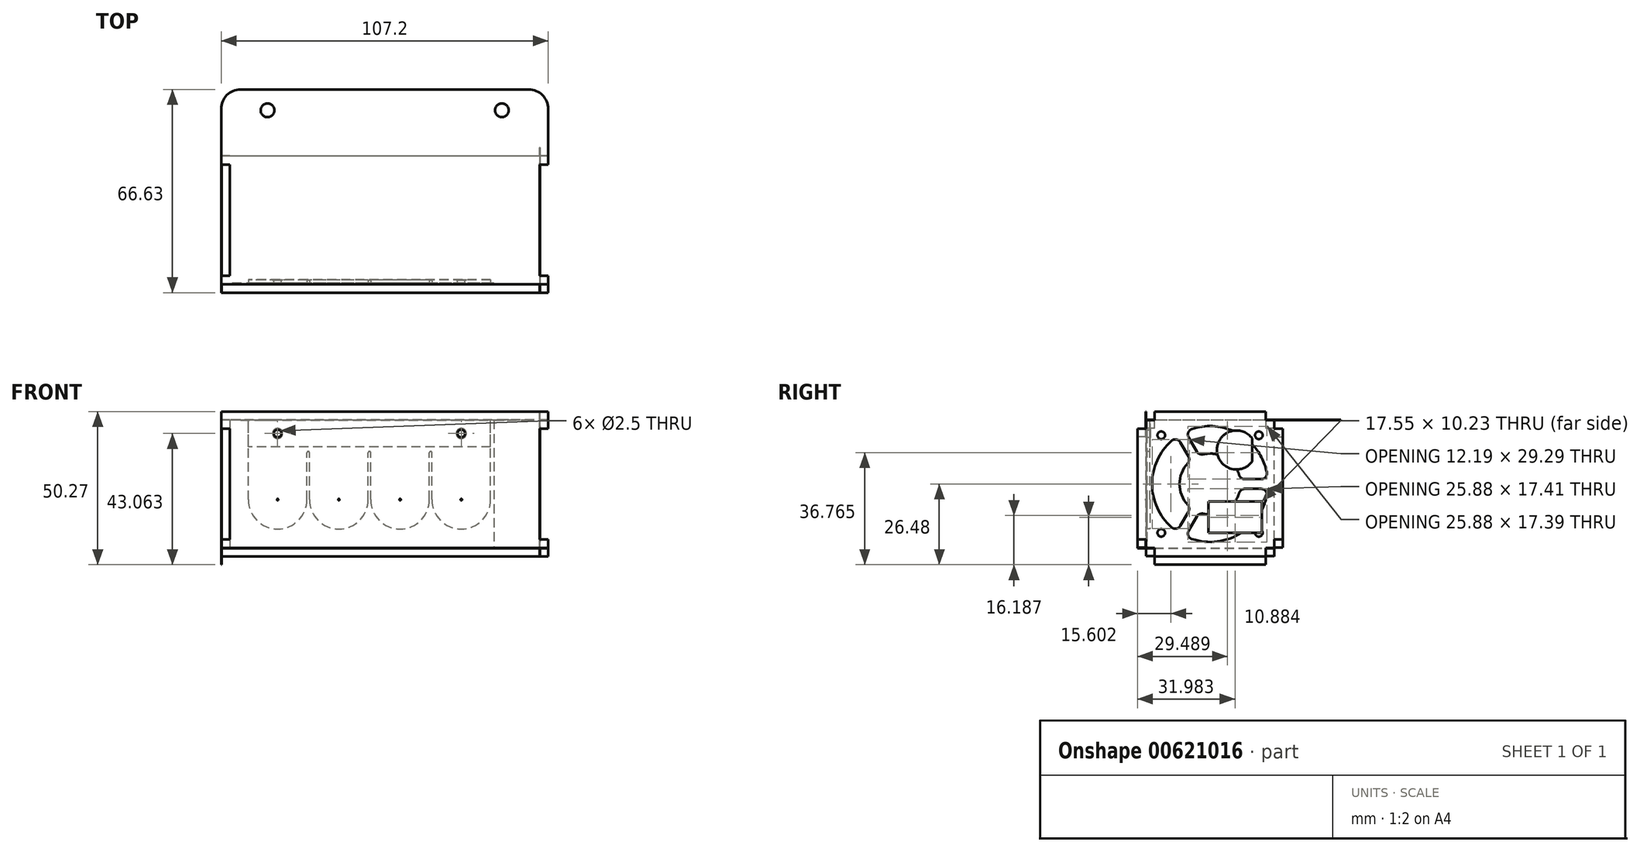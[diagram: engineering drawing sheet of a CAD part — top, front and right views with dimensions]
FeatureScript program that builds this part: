
annotation { "Feature Type Name" : "Feature", "Feature Type Description" : "" }
export const myFeature = defineFeature(function(context is Context, id is Id, definition is map)
    precondition{}
    {
        {
            assignVariable(context, id + "F0", {"name" : "et_tube_od", "anyValue" : .5});
        }
        {
            assignVariable(context, id + "F1", {"name" : "material_t", "anyValue" : .11});
        }
        {
            var Q0;
            Q0=qCreatedBy(makeId("Right.planeOp"),FACE);
            var sketch = newSketch(context, id + "F2", { "sketchPlane" : qUnion([Q0])});
            skLineSegment(sketch, "E0.bottom", {"start": v(21, -21) * mm, "end": v(-21, -21) * mm});
            skLineSegment(sketch, "E0.top", {"start": v(21, 21) * mm, "end": v(-21, 21) * mm});
            skLineSegment(sketch, "E0.left", {"start": v(21, -21) * mm, "end": v(21, 21) * mm});
            skLineSegment(sketch, "E0.right", {"start": v(-21, -21) * mm, "end": v(-21, 21) * mm});
            skPoint(sketch, "E0.middle", {"position": v(0, 0) * mm});
            skLineSegment(sketch, "E1", {"start": v(-18.2, 21) * mm, "end": v(-18.2, 23.8) * mm});
            skLineSegment(sketch, "E2", {"start": v(-18.2, 23.8) * mm, "end": v(18.2, 23.8) * mm});
            skLineSegment(sketch, "E3", {"start": v(18.2, 23.8) * mm, "end": v(18.2, 21) * mm});
            skPoint(sketch, "E4", {"position": v(0, 23.8) * mm});
            skLineSegment(sketch, "E5.MirrorCS", {"start": v(-18.2, -21) * mm, "end": v(-18.2, -23.8) * mm});
            skLineSegment(sketch, "E6.MirrorCS", {"start": v(-18.2, -23.8) * mm, "end": v(18.2, -23.8) * mm});
            skLineSegment(sketch, "E7.MirrorCS", {"start": v(18.2, -23.8) * mm, "end": v(18.2, -21) * mm});
            skLineSegment(sketch, "E8", {"start": v(21, 18.2) * mm, "end": v(23.8, 18.2) * mm});
            skLineSegment(sketch, "E9", {"start": v(23.8, 18.2) * mm, "end": v(23.8, -18.2) * mm});
            skLineSegment(sketch, "E10", {"start": v(23.8, -18.2) * mm, "end": v(21, -18.2) * mm});
            skPoint(sketch, "E11", {"position": v(23.8, 0) * mm});
            skLineSegment(sketch, "E12.MirrorCS", {"start": v(-21, 18.2) * mm, "end": v(-23.8, 18.2) * mm});
            skLineSegment(sketch, "E13.MirrorCS", {"start": v(-23.8, 18.2) * mm, "end": v(-23.8, -18.2) * mm});
            skLineSegment(sketch, "E14.MirrorCS", {"start": v(-23.8, -18.2) * mm, "end": v(-21, -18.2) * mm});
            skLineSegment(sketch, "E15", {"start": v(-16, 16) * mm, "end": v(16, 16) * mm, "construction": true});
            skLineSegment(sketch, "E16", {"start": v(16, 16) * mm, "end": v(16, -16) * mm, "construction": true});
            skLineSegment(sketch, "E17", {"start": v(16, -16) * mm, "end": v(-16, -16) * mm, "construction": true});
            skLineSegment(sketch, "E18", {"start": v(-16, -16) * mm, "end": v(-16, 16) * mm, "construction": true});
            skPoint(sketch, "E19", {"position": v(0, 16) * mm});
            skPoint(sketch, "E20", {"position": v(16, 0) * mm});
            skLineSegment(sketch, "E21", {"start": v(18.93, -1.59) * mm, "end": v(9.87, -1.59) * mm});
            skLineSegment(sketch, "E22", {"start": v(18.93, 1.59) * mm, "end": v(9.87, 1.59) * mm});
            skLineSegment(sketch, "E23", {"start": v(-3.56, -9.34) * mm, "end": v(-8.1, -17.2) * mm});
            skLineSegment(sketch, "E24", {"start": v(-10.84, -15.6) * mm, "end": v(-6.31, -7.76) * mm});
            skLineSegment(sketch, "E25", {"start": v(-6.31, 7.76) * mm, "end": v(-10.84, 15.6) * mm});
            skLineSegment(sketch, "E26", {"start": v(-8.1, 17.2) * mm, "end": v(-3.56, 9.34) * mm});
            skArc(sketch, "E27", {"start": v(-3.56, -9.34) * mm, "mid": v(5, -8.66) * mm, "end": v(9.87, -1.59) * mm});
            skArc(sketch, "E28", {"start": v(-6.31, 7.76) * mm, "mid": v(-10, 0) * mm, "end": v(-6.31, -7.76) * mm});
            skArc(sketch, "E29", {"start": v(9.87, 1.59) * mm, "mid": v(5, 8.66) * mm, "end": v(-3.56, 9.34) * mm});
            skLineSegment(sketch, "E30", {"start": v(0, 0) * mm, "end": v(-9.5, -16.45) * mm, "construction": true});
            skLineSegment(sketch, "E31", {"start": v(0, 0) * mm, "end": v(-9.5, 16.45) * mm, "construction": true});
            skLineSegment(sketch, "E32", {"start": v(0, 0) * mm, "end": v(19, 0) * mm, "construction": true});
            skLineSegment(sketch, "E33", {"start": v(-3.56, -9.34) * mm, "end": v(-6.31, -7.76) * mm, "construction": true});
            skLineSegment(sketch, "E34", {"start": v(-6.31, 7.76) * mm, "end": v(-3.56, 9.34) * mm, "construction": true});
            skLineSegment(sketch, "E35", {"start": v(9.87, -1.59) * mm, "end": v(9.87, 1.59) * mm, "construction": true});
            skPoint(sketch, "E36", {"position": v(-4.94, -8.55) * mm});
            skPoint(sketch, "E37", {"position": v(-4.94, 8.55) * mm});
            skPoint(sketch, "E38", {"position": v(9.87, 0) * mm});
            skArc(sketch, "E39", {"start": v(18.93, 1.59) * mm, "mid": v(9.5, 16.45) * mm, "end": v(-8.1, 17.2) * mm});
            skArc(sketch, "E40", {"start": v(-10.84, 15.6) * mm, "mid": v(-19, 0) * mm, "end": v(-10.84, -15.6) * mm});
            skArc(sketch, "E41", {"start": v(-8.1, -17.2) * mm, "mid": v(9.5, -16.45) * mm, "end": v(18.93, -1.59) * mm});
            skSolve(sketch);
        }
        {
            var Q0;
            Q0=makeQuery(id+"F2.imprint","IMPRINT",FACE,{"disambiguationData":[TD([[makeQuery(id+"F2.imprint","IMPRINT",EDGE,{"derivedFrom":sQuery(id+"F2.wireOp",EDGE,"yZEQATB2-qHEo-qSMK-z2fn-Af6IPuMyAryI")}),-1.0]])]});
            var Q1;
            {var subQ0=sQuery(id+"F2.wireOp",EDGE,"E1");Q1=makeQuery(id+"F2.imprint","IMPRINT",FACE,{"disambiguationData":[TD([[makeQuery(id+"F2.imprint","IMPRINT",EDGE,{"derivedFrom":subQ0}),-1.0]])]});}
            var Q2;
            {var subQ0=sQuery(id+"F2.wireOp",EDGE,"E12.MirrorCS");Q2=makeQuery(id+"F2.imprint","IMPRINT",FACE,{"disambiguationData":[TD([[makeQuery(id+"F2.imprint","IMPRINT",EDGE,{"derivedFrom":subQ0}),1.0]])]});}
            var Q3;
            {var subQ0=sQuery(id+"F2.wireOp",EDGE,"E8");Q3=makeQuery(id+"F2.imprint","IMPRINT",FACE,{"disambiguationData":[TD([[makeQuery(id+"F2.imprint","IMPRINT",EDGE,{"derivedFrom":subQ0}),-1.0]])]});}
            var Q4;
            {var subQ0=sQuery(id+"F2.wireOp",EDGE,"E5.MirrorCS");Q4=makeQuery(id+"F2.imprint","IMPRINT",FACE,{"disambiguationData":[TD([[makeQuery(id+"F2.imprint","IMPRINT",EDGE,{"derivedFrom":subQ0}),1.0]])]});}
            var Q5;
            {var subQ1=sQuery(id+"F2.wireOp",EDGE,"E0.bottom");var subQ4=sQuery(id+"F2.wireOp",EDGE,"E0.left");var subQ9=makeQuery(id+"F2.imprint","INTERSECT",VERTEX,{"derivedFrom":[subQ1,subQ4]});Q5=makeQuery(id+"F2.imprint","IMPRINT",FACE,{"disambiguationData":[TD([[makeQuery(id+"F2.imprint","IMPRINT",EDGE,{"disambiguationData":[TD([[subQ9,-1.0]])],"derivedFrom":subQ1}),-1.0]])]});}
            var Q6;
            Q6=makeQuery(id+"F2.imprint","IMPRINT",FACE,{"disambiguationData":[TD([[makeQuery(id+"F2.imprint","IMPRINT",EDGE,{"derivedFrom":sQuery(id+"F2.wireOp",EDGE,"N6NRcAgO-cwkD-j0Gi-G7g2-4PwivPb3dave")}),1.0]])]});
            var Q7;
            Q7=makeQuery(id+"F2.imprint","IMPRINT",FACE,{"disambiguationData":[TD([[makeQuery(id+"F2.imprint","IMPRINT",EDGE,{"derivedFrom":sQuery(id+"F2.wireOp",EDGE,"E21")}),1.0]])]});
            var Q8;
            Q8=makeQuery(id+"F2.imprint","IMPRINT",FACE,{"disambiguationData":[TD([[makeQuery(id+"F2.imprint","IMPRINT",EDGE,{"derivedFrom":sQuery(id+"F2.wireOp",EDGE,"E22")}),-1.0]])]});
            var Q9;
            Q9=makeQuery(id+"F2.imprint","IMPRINT",FACE,{"disambiguationData":[TD([[makeQuery(id+"F2.imprint","IMPRINT",EDGE,{"derivedFrom":sQuery(id+"F2.wireOp",EDGE,"E24")}),1.0]])]});
            extrude(context, id + "F3", {"entities" : qUnion([Q0, Q1, Q2, Q3, Q4, Q5, Q6, Q7, Q8, Q9]), "depth" : (getVariable(context, 'material_t')) * mm, "offsetDistance" : 25.4 * mm});
        }
        {
            var Q0;
            {var subQ0=sQuery(id+"F2.wireOp",EDGE,"E0.top");Q0=makeQuery(id+"F3.opExtrude","SWEPT_FACE",FACE,{"disambiguationData":[OSD([subQ0]),TDD([makeQuery(id+"F2.imprint","IMPRINT",EDGE,{"disambiguationData":[TD([[makeQuery(id+"F2.imprint","INTERSECT",VERTEX,{"derivedFrom":[subQ0,sQuery(id+"F2.wireOp",EDGE,"E0.left")]}),-1.0]])],"derivedFrom":subQ0})])]});}
            cPlane(context, id + "F4", {"entities" : qUnion([Q0]), "cplaneType" : CPlaneType.OFFSET, "offset" : 0 * mm, "width" : 152.4 * mm, "height" : 152.4 * mm});
        }
        {
            var Q0;
            Q0=qCreatedBy(id+"F4.planeOp",FACE);
            var sketch = newSketch(context, id + "F5", { "sketchPlane" : qUnion([Q0])});
            skLineSegment(sketch, "E42", {"start": v(-104.41, 23.8) * mm, "end": v(2.8, 23.8) * mm});
            skLineSegment(sketch, "E43", {"start": v(2.8, 23.8) * mm, "end": v(2.8, 18.2) * mm});
            skLineSegment(sketch, "E44", {"start": v(2.8, 18.2) * mm, "end": v(0, 18.2) * mm});
            skLineSegment(sketch, "E45", {"start": v(2.8, -21) * mm, "end": v(-104.41, -21) * mm});
            skLineSegment(sketch, "E46", {"start": v(-101.62, 18.2) * mm, "end": v(-104.41, 18.2) * mm});
            skLineSegment(sketch, "E47", {"start": v(-104.41, 18.2) * mm, "end": v(-104.41, 23.8) * mm});
            skLineSegment(sketch, "E48", {"start": v(2.8, -21) * mm, "end": v(2.8, -18.2) * mm});
            skLineSegment(sketch, "E49", {"start": v(2.8, -18.2) * mm, "end": v(0, -18.2) * mm});
            skLineSegment(sketch, "E50", {"start": v(0, -18.2) * mm, "end": v(0, 18.2) * mm});
            skLineSegment(sketch, "E51", {"start": v(-101.62, 18.2) * mm, "end": v(-101.62, -18.2) * mm});
            skLineSegment(sketch, "E52", {"start": v(-101.62, -18.2) * mm, "end": v(-104.41, -18.2) * mm});
            skLineSegment(sketch, "E53", {"start": v(-104.41, -18.2) * mm, "end": v(-104.41, -21) * mm});
            skSolve(sketch);
        }
        {
            var Q0;
            Q0=makeQuery(id+"F5.imprint","IMPRINT",FACE,{"disambiguationData":[TD([[makeQuery(id+"F5.imprint","IMPRINT",EDGE,{"derivedFrom":sQuery(id+"F5.wireOp",EDGE,"E42")}),-1.0]])]});
            extrude(context, id + "F6", {"entities" : qUnion([Q0]), "depth" : (getVariable(context, 'material_t')) * mm, "offsetDistance" : 25.4 * mm});
        }
        {
            var Q0;
            Q0=makeQuery(id+"F3.opExtrude","SWEPT_BODY",BODY,{"disambiguationData":[OSD([sQuery(id+"F2.wireOp",EDGE,"E0.bottom"),sQuery(id+"F2.wireOp",EDGE,"E0.top"),sQuery(id+"F2.wireOp",EDGE,"E0.left"),sQuery(id+"F2.wireOp",EDGE,"E0.right"),sQuery(id+"F2.wireOp",EDGE,"E1"),sQuery(id+"F2.wireOp",EDGE,"E2"),sQuery(id+"F2.wireOp",EDGE,"E3"),sQuery(id+"F2.wireOp",EDGE,"E5.MirrorCS"),sQuery(id+"F2.wireOp",EDGE,"E6.MirrorCS"),sQuery(id+"F2.wireOp",EDGE,"E7.MirrorCS"),sQuery(id+"F2.wireOp",EDGE,"E8"),sQuery(id+"F2.wireOp",EDGE,"E9"),sQuery(id+"F2.wireOp",EDGE,"E10"),sQuery(id+"F2.wireOp",EDGE,"E12.MirrorCS"),sQuery(id+"F2.wireOp",EDGE,"E13.MirrorCS"),sQuery(id+"F2.wireOp",EDGE,"E14.MirrorCS"),sQuery(id+"F2.wireOp",EDGE,"yZEQATB2-qHEo-qSMK-z2fn-Af6IPuMyAryI"),sQuery(id+"F2.wireOp",EDGE,"7anHJkbU-wOVN-GGeW-2ATg-weyE9iegAsrc"),sQuery(id+"F2.wireOp",EDGE,"JCj4ztZ3-uQRs-MAfa-rW5s-55u72G0Dj143"),sQuery(id+"F2.wireOp",EDGE,"O8wggnC7-fMfh-ZRoE-917q-eWdcVwdHsXBT")])]});
            var Q1;
            Q1=makeQuery(id+"F3.opExtrude","CAP_VERTEX",VERTEX,{"disambiguationData":[OSD([sQuery(id+"F2.wireOp",EDGE,"E1"),sQuery(id+"F2.wireOp",EDGE,"E2")])],"isStart":true});
            var Q2;
            Q2=makeQuery(id+"F6.opExtrude","CAP_VERTEX",VERTEX,{"disambiguationData":[OSD([sQuery(id+"F5.wireOp",EDGE,"E52"),sQuery(id+"F5.wireOp",EDGE,"E53")])],"isStart":false});
            transform(context, id + "F7", {"entities" : qUnion([Q0]), "transformType" : TransformType.TRANSLATION_ENTITY, "oppositeDirectionEntity" : false, "transformLine" : qUnion([Q1, Q2]), "makeCopy" : true});
        }
        {
            var Q0;
            Q0=qCreatedBy(makeId("Front.planeOp"),FACE);
            var sketch = newSketch(context, id + "F8", { "sketchPlane" : qUnion([Q0])});
            skLineSegment(sketch, "E54", {"start": v(-97.77, 0) * mm, "end": v(65.37, 0) * mm, "construction": true});
            skSolve(sketch);
        }
        {
            var Q0;
            Q0=makeQuery(id+"F6.opExtrude","SWEPT_BODY",BODY,{"disambiguationData":[OSD([sQuery(id+"F5.wireOp",EDGE,"E42"),sQuery(id+"F5.wireOp",EDGE,"E43"),sQuery(id+"F5.wireOp",EDGE,"E44"),sQuery(id+"F5.wireOp",EDGE,"E45"),sQuery(id+"F5.wireOp",EDGE,"E46"),sQuery(id+"F5.wireOp",EDGE,"E47"),sQuery(id+"F5.wireOp",EDGE,"E48"),sQuery(id+"F5.wireOp",EDGE,"E49"),sQuery(id+"F5.wireOp",EDGE,"E50"),sQuery(id+"F5.wireOp",EDGE,"E51"),sQuery(id+"F5.wireOp",EDGE,"E52"),sQuery(id+"F5.wireOp",EDGE,"E53")])]});
            var Q1;
            Q1=sQuery(id+"F8.wireOp",EDGE,"E54");
            circularPattern(context, id + "F9", {"entities" : qUnion([Q0]), "axis" : qUnion([Q1]), "angle" : 360 * degree, "instanceCount" : 4, "equalSpace" : true});
        }
        {
            var Q0;
            Q0=sQuery(id+"F2.wireOp",VERTEX,"E18.end");
            var Q1;
            Q1=sQuery(id+"F2.wireOp",VERTEX,"E18.start");
            var Q2;
            Q2=sQuery(id+"F2.wireOp",VERTEX,"E17.start");
            var Q3;
            Q3=sQuery(id+"F2.wireOp",VERTEX,"E16.start");
            var Q4;
            Q4=sQuery(id+"F11.wireOp",VERTEX,"0ce64ff8-5888-4f7d-9362-f795a0b3a2a9");
            var Q5;
            Q5=sQuery(id+"F11.wireOp",VERTEX,"a7e2b6ef-d8bb-4381-bae4-1c02abda32b3");
            var Q6;
            Q6=sQuery(id+"F11.wireOp",VERTEX,"a1c340ac-e22f-423d-a95b-deebb6622764");
            var Q7;
            Q7=makeQuery(id+"F3.opExtrude","SWEPT_BODY",BODY,{"disambiguationData":[OSD([sQuery(id+"F2.wireOp",EDGE,"E0.bottom"),sQuery(id+"F2.wireOp",EDGE,"E0.top"),sQuery(id+"F2.wireOp",EDGE,"E0.left"),sQuery(id+"F2.wireOp",EDGE,"E0.right"),sQuery(id+"F2.wireOp",EDGE,"E1"),sQuery(id+"F2.wireOp",EDGE,"E2"),sQuery(id+"F2.wireOp",EDGE,"E3"),sQuery(id+"F2.wireOp",EDGE,"E5.MirrorCS"),sQuery(id+"F2.wireOp",EDGE,"E6.MirrorCS"),sQuery(id+"F2.wireOp",EDGE,"E7.MirrorCS"),sQuery(id+"F2.wireOp",EDGE,"E8"),sQuery(id+"F2.wireOp",EDGE,"E9"),sQuery(id+"F2.wireOp",EDGE,"E10"),sQuery(id+"F2.wireOp",EDGE,"E12.MirrorCS"),sQuery(id+"F2.wireOp",EDGE,"E13.MirrorCS"),sQuery(id+"F2.wireOp",EDGE,"E14.MirrorCS")])]});
            var Q8;
            Q8=makeQuery(id+"F9.opPattern","COPY",BODY,{"derivedFrom":makeQuery(id+"F6.opExtrude","SWEPT_BODY",BODY,{"disambiguationData":[OSD([sQuery(id+"F5.wireOp",EDGE,"E42"),sQuery(id+"F5.wireOp",EDGE,"E43"),sQuery(id+"F5.wireOp",EDGE,"E44"),sQuery(id+"F5.wireOp",EDGE,"E45"),sQuery(id+"F5.wireOp",EDGE,"E46"),sQuery(id+"F5.wireOp",EDGE,"E47"),sQuery(id+"F5.wireOp",EDGE,"E48"),sQuery(id+"F5.wireOp",EDGE,"E49"),sQuery(id+"F5.wireOp",EDGE,"E50"),sQuery(id+"F5.wireOp",EDGE,"E51"),sQuery(id+"F5.wireOp",EDGE,"E52"),sQuery(id+"F5.wireOp",EDGE,"E53")])]}),"instanceName":"1"});
            hole(context, id + "F10", {"style" : HoleStyle.SIMPLE, "endStyle" : HoleEndStyle.THROUGH, "oppositeDirection" : true, "standardTappedOrClearance" : lookupTablePath({ "standard" : "ISO", "engagement" : "75%", "pitch" : "0.5 mm", "size" : "M3", "type" : "Tapped" }), "standardBlindInLast" : lookupTablePath({ "standard" : "ISO", "engagement" : "75%", "pitch" : "0.5 mm", "size" : "M3", "type" : "Tapped" }), "holeDiameter" : 2.5 * mm, "majorDiameter" : 3 * mm, "showTappedDepth" : true, "isTappedThrough" : true, "tappedDepth" : 12.7 * mm, "tapClearance" : 3, "startFromSketch" : true, "locations" : qUnion([Q0, Q1, Q2, Q3, Q4, Q5, Q6]), "scope" : qUnion([Q7, Q8])});
        }
        {
            var Q0;
            Q0=makeQuery(id+"F9.opPattern","COPY",FACE,{"derivedFrom":makeQuery(id+"F6.opExtrude","CAP_FACE",FACE,{"disambiguationData":[OSD([sQuery(id+"F5.wireOp",EDGE,"E42"),sQuery(id+"F5.wireOp",EDGE,"E43"),sQuery(id+"F5.wireOp",EDGE,"E44"),sQuery(id+"F5.wireOp",EDGE,"E45"),sQuery(id+"F5.wireOp",EDGE,"E46"),sQuery(id+"F5.wireOp",EDGE,"E47"),sQuery(id+"F5.wireOp",EDGE,"E48"),sQuery(id+"F5.wireOp",EDGE,"E49"),sQuery(id+"F5.wireOp",EDGE,"E50"),sQuery(id+"F5.wireOp",EDGE,"E51"),sQuery(id+"F5.wireOp",EDGE,"E52"),sQuery(id+"F5.wireOp",EDGE,"E53")])],"isStart":false}),"instanceName":"1"});
            var sketch = newSketch(context, id + "F11", { "sketchPlane" : qUnion([Q0])});
            skPoint(sketch, "E55", {"position": v(-85.92, -5.11) * mm});
            skPoint(sketch, "E56", {"position": v(-65.85, -5.11) * mm});
            skPoint(sketch, "E57", {"position": v(-45.77, -5.11) * mm});
            skPoint(sketch, "E58", {"position": v(-25.7, -5.11) * mm});
            skLineSegment(sketch, "E59", {"start": v(-85.92, -5.11) * mm, "end": v(-65.85, -5.11) * mm, "construction": true});
            skLineSegment(sketch, "E60", {"start": v(-45.77, -5.11) * mm, "end": v(-65.85, -5.11) * mm, "construction": true});
            skLineSegment(sketch, "E61", {"start": v(-45.77, -5.11) * mm, "end": v(-25.7, -5.11) * mm, "construction": true});
            skPoint(sketch, "E62", {"position": v(-55.8, -5.11) * mm});
            skCircle(sketch, "E63", {"center": v(-85.92, -5.11) * mm, "radius": 6.35 * mm, "construction": true});
            skLineSegment(sketch, "E64", {"start": v(0, 35.16) * mm, "end": v(-10, 35.16) * mm, "construction": true});
            skLineSegment(sketch, "E65", {"start": v(-10, 35.16) * mm, "end": v(-101.62, 35.16) * mm, "construction": true});
            skPoint(sketch, "E66", {"position": v(-55.8, 35.16) * mm});
            skLineSegment(sketch, "E67", {"start": v(-10, 35.16) * mm, "end": v(-10, -17.6) * mm, "construction": true});
            skSolve(sketch);
        }
        {
            var Q0;
            Q0=makeQuery(id+"F9.opPattern","COPY",FACE,{"derivedFrom":makeQuery(id+"F6.opExtrude","CAP_FACE",FACE,{"disambiguationData":[OSD([sQuery(id+"F5.wireOp",EDGE,"E42"),sQuery(id+"F5.wireOp",EDGE,"E43"),sQuery(id+"F5.wireOp",EDGE,"E44"),sQuery(id+"F5.wireOp",EDGE,"E45"),sQuery(id+"F5.wireOp",EDGE,"E46"),sQuery(id+"F5.wireOp",EDGE,"E47"),sQuery(id+"F5.wireOp",EDGE,"E48"),sQuery(id+"F5.wireOp",EDGE,"E49"),sQuery(id+"F5.wireOp",EDGE,"E50"),sQuery(id+"F5.wireOp",EDGE,"E51"),sQuery(id+"F5.wireOp",EDGE,"E52"),sQuery(id+"F5.wireOp",EDGE,"E53")])],"isStart":true}),"instanceName":"1"});
            var sketch = newSketch(context, id + "F12", { "sketchPlane" : qUnion([Q0])});
            skLineSegment(sketch, "E68.bottom", {"start": v(15, 21) * mm, "end": v(101.62, 21) * mm});
            skLineSegment(sketch, "E68.top", {"start": v(15, -21) * mm, "end": v(101.62, -21) * mm});
            skLineSegment(sketch, "E68.left", {"start": v(15, 21) * mm, "end": v(15, -21) * mm});
            skLineSegment(sketch, "E68.right", {"start": v(101.62, 21) * mm, "end": v(101.62, -21) * mm});
            skSolve(sketch);
        }
        {
            var Q0;
            Q0 = qSketchRegion(id + "F12", true);
            extrude(context, id + "F13", {"entities" : qUnion([Q0]), "depth" : 3 * (getVariable(context, 'material_t')) * mm, "offsetDistance" : 25.4 * mm});
        }
        {
            var Q0;
            Q0=sQuery(id+"F11.wireOp",VERTEX,"E55");
            var Q1;
            Q1=sQuery(id+"F11.wireOp",VERTEX,"E56");
            var Q2;
            Q2=sQuery(id+"F11.wireOp",VERTEX,"E57");
            var Q3;
            Q3=sQuery(id+"F11.wireOp",VERTEX,"E58");
            var Q4;
            Q4=makeQuery(id+"F9.opPattern","COPY",BODY,{"derivedFrom":makeQuery(id+"F6.opExtrude","SWEPT_BODY",BODY,{"disambiguationData":[OSD([sQuery(id+"F5.wireOp",EDGE,"E42"),sQuery(id+"F5.wireOp",EDGE,"E43"),sQuery(id+"F5.wireOp",EDGE,"E44"),sQuery(id+"F5.wireOp",EDGE,"E45"),sQuery(id+"F5.wireOp",EDGE,"E46"),sQuery(id+"F5.wireOp",EDGE,"E47"),sQuery(id+"F5.wireOp",EDGE,"E48"),sQuery(id+"F5.wireOp",EDGE,"E49"),sQuery(id+"F5.wireOp",EDGE,"E50"),sQuery(id+"F5.wireOp",EDGE,"E51"),sQuery(id+"F5.wireOp",EDGE,"E52"),sQuery(id+"F5.wireOp",EDGE,"E53")])]}),"instanceName":"1"});
            var Q5;
            Q5=makeQuery(id+"F13.opExtrude","SWEPT_BODY",BODY,{"disambiguationData":[OSD([sQuery(id+"F12.wireOp",EDGE,"E68.bottom"),sQuery(id+"F12.wireOp",EDGE,"E68.top"),sQuery(id+"F12.wireOp",EDGE,"E68.left"),sQuery(id+"F12.wireOp",EDGE,"E68.right")])]});
            hole(context, id + "F14", {"style" : HoleStyle.SIMPLE, "endStyle" : HoleEndStyle.THROUGH, "holeDiameter" : (getVariable(context, 'et_tube_od')) * mm, "majorDiameter" : 3 * mm, "isTappedThrough" : true, "tappedDepth" : 12.7 * mm, "tapClearance" : 3, "startFromSketch" : true, "locations" : qUnion([Q0, Q1, Q2, Q3]), "scope" : qUnion([Q4, Q5])});
        }
        {
            var Q0;
            Q0=makeQuery(id+"F2.imprint","IMPRINT",FACE,{"disambiguationData":[TD([[makeQuery(id+"F2.imprint","IMPRINT",EDGE,{"derivedFrom":sQuery(id+"F2.wireOp",EDGE,"E21")}),1.0]])]});
            var Q1;
            Q1=makeQuery(id+"F2.imprint","IMPRINT",FACE,{"disambiguationData":[TD([[makeQuery(id+"F2.imprint","IMPRINT",EDGE,{"derivedFrom":sQuery(id+"F2.wireOp",EDGE,"E22")}),-1.0]])]});
            var Q2;
            Q2=makeQuery(id+"F2.imprint","IMPRINT",FACE,{"disambiguationData":[TD([[makeQuery(id+"F2.imprint","IMPRINT",EDGE,{"derivedFrom":sQuery(id+"F2.wireOp",EDGE,"E24")}),1.0]])]});
            extrude(context, id + "F15", {"entities" : qUnion([Q0, Q1, Q2]), "operationType" : NewBodyOperationType.REMOVE, "endBound" : BoundingType.THROUGH_ALL, "depth" : 25.4 * mm, "offsetDistance" : 25.4 * mm});
        }
        {
            var Q0;
            Q0=makeQuery(id+"F7.opPattern","COPY",FACE,{"derivedFrom":makeQuery(id+"F3.opExtrude","CAP_FACE",FACE,{"disambiguationData":[OSD([sQuery(id+"F2.wireOp",EDGE,"E0.bottom"),sQuery(id+"F2.wireOp",EDGE,"E0.top"),sQuery(id+"F2.wireOp",EDGE,"E0.left"),sQuery(id+"F2.wireOp",EDGE,"E0.right"),sQuery(id+"F2.wireOp",EDGE,"E1"),sQuery(id+"F2.wireOp",EDGE,"E2"),sQuery(id+"F2.wireOp",EDGE,"E3"),sQuery(id+"F2.wireOp",EDGE,"E5.MirrorCS"),sQuery(id+"F2.wireOp",EDGE,"E6.MirrorCS"),sQuery(id+"F2.wireOp",EDGE,"E7.MirrorCS"),sQuery(id+"F2.wireOp",EDGE,"E8"),sQuery(id+"F2.wireOp",EDGE,"E9"),sQuery(id+"F2.wireOp",EDGE,"E10"),sQuery(id+"F2.wireOp",EDGE,"E12.MirrorCS"),sQuery(id+"F2.wireOp",EDGE,"E13.MirrorCS"),sQuery(id+"F2.wireOp",EDGE,"E14.MirrorCS")])],"isStart":true}),"instanceName":"1"});
            var sketch = newSketch(context, id + "F16", { "sketchPlane" : qUnion([Q0])});
            skArc(sketch, "E69", {"start": v(-13.82, 7.38) * mm, "mid": v(-2.26, 11.18) * mm, "end": v(-13.82, 14.97) * mm});
            skLineSegment(sketch, "E70", {"start": v(-13.82, 7.38) * mm, "end": v(-13.82, 14.97) * mm});
            skLineSegment(sketch, "E71.bottom", {"start": v(-16.97, -16) * mm, "end": v(0.58, -16) * mm});
            skLineSegment(sketch, "E71.top", {"start": v(-16.97, -5.76) * mm, "end": v(0.58, -5.76) * mm});
            skLineSegment(sketch, "E71.left", {"start": v(-16.97, -16) * mm, "end": v(-16.97, -5.76) * mm});
            skLineSegment(sketch, "E71.right", {"start": v(0.58, -16) * mm, "end": v(0.58, -5.76) * mm});
            skSolve(sketch);
        }
        {
            var Q0;
            Q0 = qSketchRegion(id + "F16", true);
            extrude(context, id + "F17", {"entities" : qUnion([Q0]), "operationType" : NewBodyOperationType.REMOVE, "endBound" : BoundingType.THROUGH_ALL, "oppositeDirection" : true, "depth" : 25.4 * mm, "offsetDistance" : 25.4 * mm});
        }
        {
            var Q0;
            Q0=makeQuery(id+"F15.boolean.opBoolean","COPY",EDGE,{"derivedFrom":makeQuery(id+"F15.opExtrude","SWEPT_EDGE",EDGE,{"disambiguationData":[OSD([sQuery(id+"F2.wireOp",EDGE,"E22"),sQuery(id+"F2.wireOp",EDGE,"E29")])]})});
            var Q1;
            Q1=makeQuery(id+"F15.boolean.opBoolean","COPY",EDGE,{"derivedFrom":makeQuery(id+"F15.opExtrude","SWEPT_EDGE",EDGE,{"disambiguationData":[OSD([sQuery(id+"F2.wireOp",EDGE,"E26"),sQuery(id+"F2.wireOp",EDGE,"E29")])]})});
            var Q2;
            Q2=makeQuery(id+"F15.boolean.opBoolean","COPY",EDGE,{"derivedFrom":makeQuery(id+"F15.opExtrude","SWEPT_EDGE",EDGE,{"disambiguationData":[OSD([sQuery(id+"F2.wireOp",EDGE,"E23"),sQuery(id+"F2.wireOp",EDGE,"E41")])]})});
            var Q3;
            Q3=makeQuery(id+"F15.boolean.opBoolean","COPY",EDGE,{"derivedFrom":makeQuery(id+"F15.opExtrude","SWEPT_EDGE",EDGE,{"disambiguationData":[OSD([sQuery(id+"F2.wireOp",EDGE,"E25"),sQuery(id+"F2.wireOp",EDGE,"E40")])]})});
            var Q4;
            Q4=makeQuery(id+"F15.boolean.opBoolean","COPY",EDGE,{"derivedFrom":makeQuery(id+"F15.opExtrude","SWEPT_EDGE",EDGE,{"disambiguationData":[OSD([sQuery(id+"F2.wireOp",EDGE,"E24"),sQuery(id+"F2.wireOp",EDGE,"E28")])]})});
            var Q5;
            Q5=makeQuery(id+"F15.boolean.opBoolean","COPY",EDGE,{"derivedFrom":makeQuery(id+"F15.opExtrude","SWEPT_EDGE",EDGE,{"disambiguationData":[OSD([sQuery(id+"F2.wireOp",EDGE,"E21"),sQuery(id+"F2.wireOp",EDGE,"E41")])]})});
            var Q6;
            Q6=makeQuery(id+"F15.boolean.opBoolean","COPY",EDGE,{"derivedFrom":makeQuery(id+"F15.opExtrude","SWEPT_EDGE",EDGE,{"disambiguationData":[OSD([sQuery(id+"F2.wireOp",EDGE,"E21"),sQuery(id+"F2.wireOp",EDGE,"E27")])]})});
            var Q7;
            Q7=makeQuery(id+"F15.boolean.opBoolean","COPY",EDGE,{"derivedFrom":makeQuery(id+"F15.opExtrude","SWEPT_EDGE",EDGE,{"disambiguationData":[OSD([sQuery(id+"F2.wireOp",EDGE,"E23"),sQuery(id+"F2.wireOp",EDGE,"E27")])]})});
            var Q8;
            Q8=makeQuery(id+"F15.boolean.opBoolean","COPY",EDGE,{"derivedFrom":makeQuery(id+"F15.opExtrude","SWEPT_EDGE",EDGE,{"disambiguationData":[OSD([sQuery(id+"F2.wireOp",EDGE,"E26"),sQuery(id+"F2.wireOp",EDGE,"E39")])]})});
            var Q9;
            Q9=makeQuery(id+"F15.boolean.opBoolean","COPY",EDGE,{"derivedFrom":makeQuery(id+"F15.opExtrude","SWEPT_EDGE",EDGE,{"disambiguationData":[OSD([sQuery(id+"F2.wireOp",EDGE,"E24"),sQuery(id+"F2.wireOp",EDGE,"E40")])]})});
            var Q10;
            Q10=makeQuery(id+"F15.boolean.opBoolean","COPY",EDGE,{"derivedFrom":makeQuery(id+"F15.opExtrude","SWEPT_EDGE",EDGE,{"disambiguationData":[OSD([sQuery(id+"F2.wireOp",EDGE,"E25"),sQuery(id+"F2.wireOp",EDGE,"E28")])]})});
            var Q11;
            Q11=makeQuery(id+"F15.boolean.opBoolean","COPY",EDGE,{"derivedFrom":makeQuery(id+"F15.opExtrude","SWEPT_EDGE",EDGE,{"disambiguationData":[OSD([sQuery(id+"F2.wireOp",EDGE,"E22"),sQuery(id+"F2.wireOp",EDGE,"E39")])]})});
            fillet(context, id + "F18", {"entities" : qUnion([Q0, Q1, Q2, Q3, Q4, Q5, Q6, Q7, Q8, Q9, Q10, Q11]), "radius" : 1.9 * mm, "tangentPropagation" : true, "allowEdgeOverflow" : false});
        }
        {
            var Q0;
            Q0=makeQuery(id+"F6.opExtrude","SWEPT_FACE",FACE,{"disambiguationData":[OSD([sQuery(id+"F5.wireOp",EDGE,"E42")])]});
            extrude(context, id + "F19", {"entities" : qUnion([Q0]), "operationType" : NewBodyOperationType.ADD, "depth" : 19.05 * mm, "offsetDistance" : 25.4 * mm});
        }
        {
            var Q0;
            Q0=makeQuery(id+"F19.opExtrude","CAP_EDGE",EDGE,{"disambiguationData":[OSD([sQuery(id+"F5.wireOp",EDGE,"E42"),sQuery(id+"F5.wireOp",EDGE,"E43")])],"isStart":false});
            var Q1;
            Q1=makeQuery(id+"F19.opExtrude","CAP_EDGE",EDGE,{"disambiguationData":[OSD([sQuery(id+"F5.wireOp",EDGE,"E42"),sQuery(id+"F5.wireOp",EDGE,"E47")])],"isStart":false});
            fillet(context, id + "F20", {"entities" : qUnion([Q0, Q1]), "radius" : 6.35 * mm, "tangentPropagation" : true, "allowEdgeOverflow" : false});
        }
        {
            var Q0;
            {var subQ0=sQuery(id+"F5.wireOp",EDGE,"E42");Q0=makeQuery(id+"F19.boolean.opBoolean","MERGE",FACE,{"derivedFrom":[makeQuery(id+"F6.opExtrude","CAP_FACE",FACE,{"disambiguationData":[OSD([subQ0,sQuery(id+"F5.wireOp",EDGE,"E43"),sQuery(id+"F5.wireOp",EDGE,"E44"),sQuery(id+"F5.wireOp",EDGE,"E45"),sQuery(id+"F5.wireOp",EDGE,"E46"),sQuery(id+"F5.wireOp",EDGE,"E47"),sQuery(id+"F5.wireOp",EDGE,"E48"),sQuery(id+"F5.wireOp",EDGE,"E49"),sQuery(id+"F5.wireOp",EDGE,"E50"),sQuery(id+"F5.wireOp",EDGE,"E51"),sQuery(id+"F5.wireOp",EDGE,"E52"),sQuery(id+"F5.wireOp",EDGE,"E53")])],"isStart":true}),makeQuery(id+"F19.opExtrude","SWEPT_FACE",FACE,{"disambiguationData":[OSD([subQ0]),TDD([makeQuery(id+"F6.opExtrude","CAP_EDGE",EDGE,{"disambiguationData":[OSD([subQ0])],"isStart":true})])]})]});}
            var sketch = newSketch(context, id + "F21", { "sketchPlane" : qUnion([Q0])});
            skPoint(sketch, "E72", {"position": v(-12.37, -36.01) * mm});
            skPoint(sketch, "E73", {"position": v(-89.24, -36.01) * mm});
            skLineSegment(sketch, "E74", {"start": v(-12.37, -36.01) * mm, "end": v(-89.24, -36.01) * mm, "construction": true});
            skPoint(sketch, "E75", {"position": v(-50.8, -36.01) * mm});
            skPoint(sketch, "E76", {"position": v(-50.8, -42.84) * mm});
            skLineSegment(sketch, "E77", {"start": v(-50.8, -42.84) * mm, "end": v(-50.8, -23.8) * mm, "construction": true});
            skSolve(sketch);
        }
        {
            var Q0;
            Q0=sQuery(id+"F21.wireOp",VERTEX,"E72");
            var Q1;
            Q1=sQuery(id+"F21.wireOp",VERTEX,"E73");
            var Q2;
            Q2=makeQuery(id+"F6.opExtrude","SWEPT_BODY",BODY,{"disambiguationData":[OSD([sQuery(id+"F5.wireOp",EDGE,"E42"),sQuery(id+"F5.wireOp",EDGE,"E43"),sQuery(id+"F5.wireOp",EDGE,"E44"),sQuery(id+"F5.wireOp",EDGE,"E45"),sQuery(id+"F5.wireOp",EDGE,"E46"),sQuery(id+"F5.wireOp",EDGE,"E47"),sQuery(id+"F5.wireOp",EDGE,"E48"),sQuery(id+"F5.wireOp",EDGE,"E49"),sQuery(id+"F5.wireOp",EDGE,"E50"),sQuery(id+"F5.wireOp",EDGE,"E51"),sQuery(id+"F5.wireOp",EDGE,"E52"),sQuery(id+"F5.wireOp",EDGE,"E53")])]});
            hole(context, id + "F22", {"style" : HoleStyle.SIMPLE, "endStyle" : HoleEndStyle.THROUGH, "standardTappedOrClearance" : lookupTablePath({ "standard" : "ANSI", "fit" : "Normal (ASME)", "size" : "#8", "type" : "Clearance" }), "standardBlindInLast" : lookupTablePath({ "fit" : "Free", "standard" : "ANSI", "size" : "#8", "type" : "Clearance" }), "holeDiameter" : 4.5 * mm, "majorDiameter" : 6.35 * mm, "isTappedThrough" : true, "tappedDepth" : 12.7 * mm, "tapClearance" : 3, "startFromSketch" : true, "locations" : qUnion([Q0, Q1]), "scope" : qUnion([Q2])});
        }
        {
            var Q0;
            Q0=makeQuery(id+"F13.opExtrude","CAP_FACE",FACE,{"disambiguationData":[OSD([sQuery(id+"F12.wireOp",EDGE,"E68.bottom"),sQuery(id+"F12.wireOp",EDGE,"E68.top"),sQuery(id+"F12.wireOp",EDGE,"E68.left"),sQuery(id+"F12.wireOp",EDGE,"E68.right")])],"isStart":false});
            var sketch = newSketch(context, id + "F23", { "sketchPlane" : qUnion([Q0])});
            skLineSegment(sketch, "E78.0", {"start": v(-2.8, 21) * mm, "end": v(104.41, 21) * mm, "construction": true});
            skArc(sketch, "E79", {"start": v(16.07, -5.11) * mm, "mid": v(25.7, -14.74) * mm, "end": v(35.33, -5.11) * mm});
            skArc(sketch, "E80", {"start": v(36.15, -5.11) * mm, "mid": v(45.77, -14.74) * mm, "end": v(55.4, -5.11) * mm});
            skArc(sketch, "E81", {"start": v(56.22, -5.11) * mm, "mid": v(65.85, -14.74) * mm, "end": v(75.47, -5.11) * mm});
            skArc(sketch, "E82", {"start": v(76.3, -5.11) * mm, "mid": v(85.92, -14.74) * mm, "end": v(95.54, -5.11) * mm});
            skLineSegment(sketch, "E83", {"start": v(16.07, -5.11) * mm, "end": v(16.07, 10.29) * mm});
            skLineSegment(sketch, "E84", {"start": v(35.33, -5.11) * mm, "end": v(35.33, 10.29) * mm});
            skLineSegment(sketch, "E85", {"start": v(36.15, -5.11) * mm, "end": v(36.15, 10.29) * mm});
            skLineSegment(sketch, "E86", {"start": v(55.4, -5.11) * mm, "end": v(55.4, 10.29) * mm});
            skLineSegment(sketch, "E87", {"start": v(56.22, -5.11) * mm, "end": v(56.22, 10.29) * mm});
            skLineSegment(sketch, "E88", {"start": v(75.47, -5.11) * mm, "end": v(75.47, 10.29) * mm});
            skLineSegment(sketch, "E89", {"start": v(76.3, -5.11) * mm, "end": v(76.3, 10.29) * mm});
            skLineSegment(sketch, "E90", {"start": v(95.54, -5.11) * mm, "end": v(95.54, 10.29) * mm});
            skArc(sketch, "E91", {"start": v(35.33, 10.29) * mm, "mid": v(35.74, 10.7) * mm, "end": v(36.15, 10.29) * mm});
            skArc(sketch, "E92", {"start": v(55.4, 10.29) * mm, "mid": v(55.8, 10.7) * mm, "end": v(56.22, 10.29) * mm});
            skArc(sketch, "E93", {"start": v(75.47, 10.29) * mm, "mid": v(75.88, 10.7) * mm, "end": v(76.3, 10.29) * mm});
            skLineSegment(sketch, "E94", {"start": v(16.07, 10.29) * mm, "end": v(16.07, 21) * mm});
            skLineSegment(sketch, "E95", {"start": v(16.07, 21) * mm, "end": v(95.54, 21) * mm});
            skPoint(sketch, "E95.endSnap0", {"position": v(103.01, 18.2) * mm});
            skLineSegment(sketch, "E96", {"start": v(95.54, 21) * mm, "end": v(95.54, 10.29) * mm});
            skPoint(sketch, "E97", {"position": v(25.7, 16.58) * mm});
            skPoint(sketch, "E98", {"position": v(45.77, 16.58) * mm});
            skPoint(sketch, "E99", {"position": v(65.85, 16.58) * mm});
            skPoint(sketch, "E100", {"position": v(85.92, 16.58) * mm});
            skPoint(sketch, "E101.0", {"position": v(55.8, 35.16) * mm});
            skSolve(sketch);
        }
        {
            var Q0;
            Q0 = qSketchRegion(id + "F23", true);
            extrude(context, id + "F24", {"entities" : qUnion([Q0]), "depth" : 1 * mm, "offsetDistance" : 25.4 * mm});
        }
        {
            var Q0;
            Q0=makeQuery(id+"F24.opExtrude","CAP_FACE",FACE,{"disambiguationData":[OSD([sQuery(id+"F23.wireOp",EDGE,"E79"),sQuery(id+"F23.wireOp",EDGE,"E80"),sQuery(id+"F23.wireOp",EDGE,"E81"),sQuery(id+"F23.wireOp",EDGE,"E82"),sQuery(id+"F23.wireOp",EDGE,"E83"),sQuery(id+"F23.wireOp",EDGE,"E84"),sQuery(id+"F23.wireOp",EDGE,"E85"),sQuery(id+"F23.wireOp",EDGE,"E86"),sQuery(id+"F23.wireOp",EDGE,"E87"),sQuery(id+"F23.wireOp",EDGE,"E88"),sQuery(id+"F23.wireOp",EDGE,"E89"),sQuery(id+"F23.wireOp",EDGE,"E90"),sQuery(id+"F23.wireOp",EDGE,"E91"),sQuery(id+"F23.wireOp",EDGE,"E92"),sQuery(id+"F23.wireOp",EDGE,"E93"),sQuery(id+"F23.wireOp",EDGE,"E94"),sQuery(id+"F23.wireOp",EDGE,"E95"),sQuery(id+"F23.wireOp",EDGE,"E96")])],"isStart":false});
            var sketch = newSketch(context, id + "F25", { "sketchPlane" : qUnion([Q0])});
            skPoint(sketch, "E102.0", {"position": v(25.7, 16.58) * mm});
            skPoint(sketch, "E102.1", {"position": v(45.77, 16.58) * mm});
            skPoint(sketch, "E102.2", {"position": v(65.85, 16.58) * mm});
            skPoint(sketch, "E102.3", {"position": v(85.92, 16.58) * mm});
            skLineSegment(sketch, "E103.bottom", {"start": v(16.07, 21) * mm, "end": v(95.54, 21) * mm});
            skLineSegment(sketch, "E103.top", {"start": v(16.07, 12.17) * mm, "end": v(95.54, 12.17) * mm});
            skLineSegment(sketch, "E103.left", {"start": v(16.07, 21) * mm, "end": v(16.07, 12.17) * mm});
            skLineSegment(sketch, "E103.right", {"start": v(95.54, 21) * mm, "end": v(95.54, 12.17) * mm});
            skPoint(sketch, "E104", {"position": v(16.07, 16.58) * mm});
            skSolve(sketch);
        }
        {
            var Q0;
            Q0 = qSketchRegion(id + "F25", true);
            extrude(context, id + "F26", {"entities" : qUnion([Q0]), "depth" : (getVariable(context, 'material_t')) * mm, "offsetDistance" : 25.4 * mm});
        }
        {
            var Q0;
            Q0=sQuery(id+"F25.wireOp",VERTEX,"E102.0");
            var Q1;
            Q1=sQuery(id+"F25.wireOp",VERTEX,"E102.3");
            var Q2;
            Q2=makeQuery(id+"F9.opPattern","COPY",BODY,{"derivedFrom":makeQuery(id+"F6.opExtrude","SWEPT_BODY",BODY,{"disambiguationData":[OSD([sQuery(id+"F5.wireOp",EDGE,"E42"),sQuery(id+"F5.wireOp",EDGE,"E43"),sQuery(id+"F5.wireOp",EDGE,"E44"),sQuery(id+"F5.wireOp",EDGE,"E45"),sQuery(id+"F5.wireOp",EDGE,"E46"),sQuery(id+"F5.wireOp",EDGE,"E47"),sQuery(id+"F5.wireOp",EDGE,"E48"),sQuery(id+"F5.wireOp",EDGE,"E49"),sQuery(id+"F5.wireOp",EDGE,"E50"),sQuery(id+"F5.wireOp",EDGE,"E51"),sQuery(id+"F5.wireOp",EDGE,"E52"),sQuery(id+"F5.wireOp",EDGE,"E53")])]}),"instanceName":"1"});
            var Q3;
            Q3=makeQuery(id+"F24.opExtrude","SWEPT_BODY",BODY,{"disambiguationData":[OSD([sQuery(id+"F23.wireOp",EDGE,"E79"),sQuery(id+"F23.wireOp",EDGE,"E80"),sQuery(id+"F23.wireOp",EDGE,"E81"),sQuery(id+"F23.wireOp",EDGE,"E82"),sQuery(id+"F23.wireOp",EDGE,"E83"),sQuery(id+"F23.wireOp",EDGE,"E84"),sQuery(id+"F23.wireOp",EDGE,"E85"),sQuery(id+"F23.wireOp",EDGE,"E86"),sQuery(id+"F23.wireOp",EDGE,"E87"),sQuery(id+"F23.wireOp",EDGE,"E88"),sQuery(id+"F23.wireOp",EDGE,"E89"),sQuery(id+"F23.wireOp",EDGE,"E90"),sQuery(id+"F23.wireOp",EDGE,"E91"),sQuery(id+"F23.wireOp",EDGE,"E92"),sQuery(id+"F23.wireOp",EDGE,"E93"),sQuery(id+"F23.wireOp",EDGE,"E94"),sQuery(id+"F23.wireOp",EDGE,"E95"),sQuery(id+"F23.wireOp",EDGE,"E96")])]});
            var Q4;
            Q4=makeQuery(id+"F13.opExtrude","SWEPT_BODY",BODY,{"disambiguationData":[OSD([sQuery(id+"F12.wireOp",EDGE,"E68.bottom"),sQuery(id+"F12.wireOp",EDGE,"E68.top"),sQuery(id+"F12.wireOp",EDGE,"E68.left"),sQuery(id+"F12.wireOp",EDGE,"E68.right")])]});
            hole(context, id + "F27", {"style" : HoleStyle.SIMPLE, "endStyle" : HoleEndStyle.THROUGH, "standardTappedOrClearance" : lookupTablePath({ "standard" : "ISO", "engagement" : "75%", "pitch" : "0.5 mm", "size" : "M3", "type" : "Tapped" }), "standardBlindInLast" : lookupTablePath({ "standard" : "ISO", "engagement" : "75%", "pitch" : "0.5 mm", "size" : "M3", "type" : "Tapped" }), "holeDiameter" : 2.5 * mm, "majorDiameter" : 3 * mm, "showTappedDepth" : true, "isTappedThrough" : true, "tappedDepth" : 12.7 * mm, "tapClearance" : 3, "startFromSketch" : true, "locations" : qUnion([Q0, Q1]), "scope" : qUnion([Q2, Q3, Q4])});
        }
        {
            var Q0;
            Q0=sQuery(id+"F25.wireOp",VERTEX,"E102.0");
            var Q1;
            Q1=sQuery(id+"F25.wireOp",VERTEX,"E102.3");
            var Q2;
            Q2=makeQuery(id+"F26.opExtrude","SWEPT_BODY",BODY,{"disambiguationData":[OSD([sQuery(id+"F25.wireOp",EDGE,"E103.bottom"),sQuery(id+"F25.wireOp",EDGE,"E103.top"),sQuery(id+"F25.wireOp",EDGE,"E103.left"),sQuery(id+"F25.wireOp",EDGE,"E103.right")])]});
            hole(context, id + "F28", {"style" : HoleStyle.SIMPLE, "endStyle" : HoleEndStyle.THROUGH, "oppositeDirection" : true, "standardTappedOrClearance" : lookupTablePath({ "standard" : "ISO", "fit" : "Normal", "size" : "M3", "type" : "Clearance" }), "standardBlindInLast" : lookupTablePath({ "fit" : "Standard", "standard" : "ISO", "size" : "M3", "type" : "Clearance" }), "holeDiameter" : 3.3 * mm, "majorDiameter" : 3 * mm, "isTappedThrough" : true, "tappedDepth" : 12.7 * mm, "tapClearance" : 3, "startFromSketch" : true, "locations" : qUnion([Q0, Q1]), "scope" : qUnion([Q2])});
        }
    });
